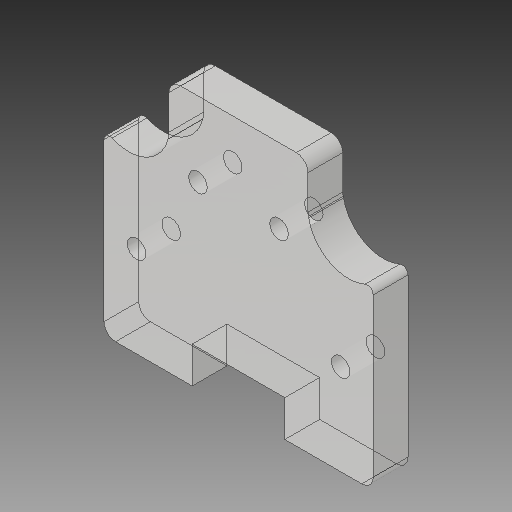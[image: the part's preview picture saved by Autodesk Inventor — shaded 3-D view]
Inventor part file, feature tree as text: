
AUTODESK INVENTOR PART (.ipt)
format: ipt  version: 2018 (Build 220112000, 112)  size: 166,912 bytes
history: native  units: mm
features: sketch x4, other x3, plane x1
ambient origin geometry x8: Origin, YZ Plane, XZ Plane, XY Plane, X Axis, Y Axis, Z Axis, Center Point
bodies: Solid1 (feature_tree)
feature tree (8):
  other  "Hotend Slide Part3.ipt"
  other  "Solid1::Hotend Slide Part3.ipt"
  other  "TaggingFeature1"
  sketch  "Sketch1"  dims[d0=10.0mm]
  sketch  "Sketch2"
  sketch  "Sketch3"
  sketch  "Sketch4"
  plane  "Work Plane1"
